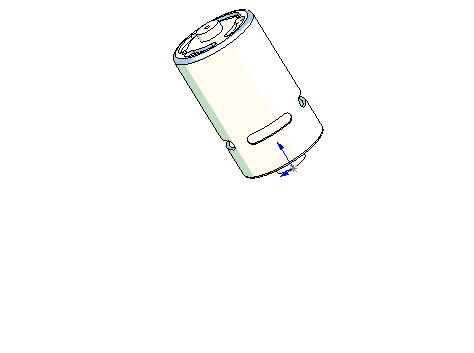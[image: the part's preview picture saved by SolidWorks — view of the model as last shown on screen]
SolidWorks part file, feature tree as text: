
SOLIDWORKS PART (.sldprt)
format: sldprt  version: not decoded by parser v0  size: 387,584 bytes
history: native  units: mm
features: plane x8, fillet x3, cut_extrude x2, sketch x1, revolve x1, pattern_circular x1 + 13 further entries (+7 scaffold rows collapsed)
feature tree (36):
  scaffold x7  (default folders/planes/origin — collapsed)
  "Corps de surface"
  plane  "Face"
  "Dessus"
  "Droite"
  sketch  "Esquisse1"
  "param"
  plane  "gss_2demu_pline1"
  "param"
  plane  "gss_2demu_pline2"
  "param"
  plane  "gss_2demu_pline3"
  "param"
  plane  "gss_2demu_pline4"
  "param"
  plane  "gss_2demu_pline5"
  "param"
  plane  "gss_2demu_pline6"
  "param"
  plane  "gss_2demu_pline7"
  "param"
  revolve  "Révolution1"  Angle=360deg
  fillet  "Congé1"  Radius=2mm
  fillet  "Congé2"  Radius=1mm
  "Esquisse2"
  cut_extrude  "Enlèv. mat.-Extru.1"  [1 undecoded]
  fillet  "Congé3"  Radius=0.5mm
  "Esquisse3"
  cut_extrude  "Enlèv. mat.-Extru.2"  Depth=100mm
  pattern_circular  "Répétition circulaire1"  Count=2 Angle=90deg
decode coverage: 6 of 8 modeling features carry decoded parameters; 13 rows unclassified (native names shown)
note: 1 parameter value undecoded
note: suppression state not decoded; provenance and decode notes live in map.json
